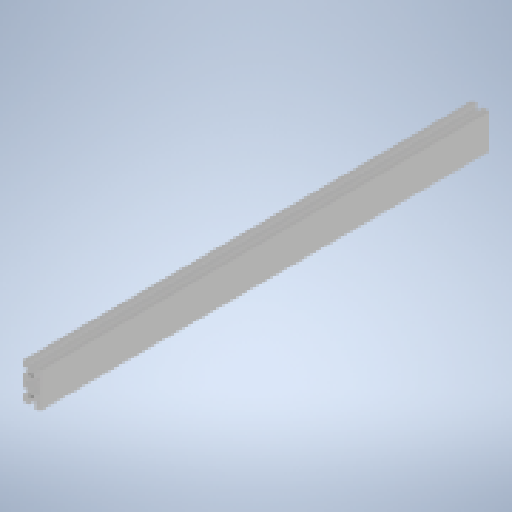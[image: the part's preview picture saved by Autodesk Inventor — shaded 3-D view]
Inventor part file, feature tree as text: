
AUTODESK INVENTOR PART (.ipt)
format: ipt  version: 2024 (Build 280153000, 153)  size: 393,216 bytes
history: native  units: mm
features: other x7, thread x4, sketch x2, extrude x1, hole x1, pattern_linear x1
ambient origin geometry x8: Origin, YZ Plane, XZ Plane, XY Plane, X Axis, Y Axis, Z Axis, Center Point
bodies: Solid1 (feature_tree)
feature tree (16):
  extrude  "Extrusion1"  Depth=20.0mm TaperAngle=0.0deg
  hole  "Hole1"  [1 undecoded]
  pattern_linear  "Rectangular Pattern1"  Spacing1=10.0mm  [1 undecoded]
  other  "C1_XY"
  other  "C1_YZ"
  other  "C1_ZX"
  other  "C1_X"
  other  "C1_Y"
  other  "C1_Z"
  other  "C1_Center"
  thread  "Thread1"  [1 undecoded]
  thread  "Thread2"  [1 undecoded]
  thread  "Thread3"  [1 undecoded]
  thread  "Thread4"  [1 undecoded]
  sketch  "Sketch_63"  dims[d2=4.2mm d3=6.0mm d4=4.0mm d5=2.0mm d6=90.0deg d7=425.0mm d8=0.0mm d9=20.0mm d11=20.0mm d12=10.0mm d14=0.0mm d15=0.0mm d16=10.0mm d17=0.0mm d18=10.0mm d19=0.0mm d20=10.0mm d21=0.0mm d22=10.0mm d23=0.0mm]
  sketch  "Sketch2"  dims[d0=425.0mm d1=0.0mm]
note: 6 required parameter values undecoded (feature->parameter linkage not recoverable at this tier; creation-order binding heuristic only, values carry confidence <= 0.55)
